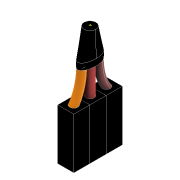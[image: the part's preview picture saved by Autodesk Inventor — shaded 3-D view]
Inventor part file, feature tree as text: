
AUTODESK INVENTOR PART (.ipt)
format: ipt  version: 2022 (Build 260153000, 153)  size: 378,368 bytes
history: native  units: mm
features: sketch x11, extrude x4, plane x3, projected_geometry x3, sweep x2, split x1, loft x1, other x1
ambient origin geometry x8: Origin, YZ Plane, XZ Plane, XY Plane, X Axis, Y Axis, Z Axis, Center Point
bodies: Solid1 (feature_tree), Solid4 (feature_tree), Solid2 (feature_tree), Solid3 (feature_tree)
feature tree (26):
  extrude  "Extrusion1"  Depth=10.0mm TaperAngle=0.0deg
  extrude  "Extrusion2"  Depth=1.3mm
  sketch  "Sketch3"  dims[d12=1.3mm d13=1.3mm]
  plane  "Work Plane1"
  sweep  "Sweep1"
  sweep  "Sweep2"
  extrude  "Extrusion3"  TaperAngle=0.0deg  [1 undecoded]
  split  "Split1"
  plane  "Work Plane2"
  extrude  "Extrusion4"  Depth=5.0mm
  plane  "Work Plane3"
  loft  "Loft1"
  sketch  "Sketch11"  dims[d35=-5.0mm d36=1.88mm d37=0.0mm d38=90.0deg d39=0.0mm d40=90.0deg]
  sketch  "Sketch1"  dims[d0=30.0mm d2=2.55mm d3=10.0mm d5=10.0mm d7=7.0mm d8=0.0mm]
  sketch  "Sketch2"  dims[d9=1.0mm d10=0.0mm d11=1.3mm]
  projected_geometry  "Projected Loop1"
  projected_geometry  "Projected Loop2"
  projected_geometry  "Projected Loop3"
  sketch  "Sketch4"  dims[d14=5.0mm d15=1.3mm]
  sketch  "Sketch5"  dims[d16=2.6mm d17=0.0mm d18=0.0mm]
  sketch  "Sketch6"  dims[d19=1.3mm d20=1.3mm d21=1.3mm d22=5.0mm d23=1.3mm d24=2.6mm]
  sketch  "Sketch7"  dims[d25=0.0mm d26=0.0mm d27=1.3mm d28=1.3mm d29=1.3mm]
  sketch  "Sketch8"  dims[d30=5.0mm d31=0.0mm]
  sketch  "Sketch9"  dims[d32=4.5mm]
  sketch  "Sketch10"  dims[d33=1.0mm d34=0.0mm]
  other  "Edges1"
note: 1 required parameter value undecoded (feature->parameter linkage not recoverable at this tier; creation-order binding heuristic only, values carry confidence <= 0.55)
